# Revit family: Electronics_Monitors_Biamp_Vocia_End-Of-Line-Device_ELD-1__
name_source: partatom
category: Communication Devices
units: mm (PartAtom-declared; Revit-internal decimal feet)

## family parameters
Cut with Voids When Loaded = No
Host = Face
Maintain Annotation Orientation = No
OmniClass Number = 23.85.10.11.11
OmniClass Title = Sound and Signal Devices
Part Type = Normal
Room Calculation Point = No
Round Connector Dimension = Use Diameter
Shared = No

## types (1)
- ELD-1
    Altitude = 0-10,000 ft (0-3000m) MSL
    Apparent Load = 0 VA
    Compliance = CE marked (Europe), RoHS Directive (Europe), RINA (Italy)
    Connector Description = PoE 802.3af Class 1
    Default Elevation = 48 "
    Depth = 3.1 "
    Description = Vocia® ELD-1 End Of Line Device
    Height = 1.1 "
    Housing Material = Biamp - Metal - Silver
    Humidity = 0-95% relative humidity (non-condensing)
    Manufacturer = Biamp
    Max Input Level = Adjustable in 1dB steps over a 30dB range
    Max Power Consumption = 0 W
    Model = Vocia ELD-1
    Network Connection = RJ45 with Ethernet (CAT5, CAT5e, CAT6 or CAT7)
    Number of Poles = 1
    Power Factor = 1
    Product Documentation Link = https://downloads.biamp.com
    Product Page URL = https://www.biamp.com
    Product data url = https://www.bimobject.com
    Speaker Line Input Configuration = Balanced and Floating (transformer coupled)
    Speaker Line Input Impedance = 70/100V Input: >100 kohm; Low-Z Input: 10 kohm
    System Headroom = 70/100V Input: 200V; Low-Z Input: 100V
    Temperature Range = 32 - 108° F (0 - 42° C)
    URL = https://www.biamp.com
    Voltage = 0 V
    Weight = 0.66 lbf
    Width = 6 "

## geometry (parser evidence)
native form markers: Sweep x2
no freeform markers — native parametric forms only
